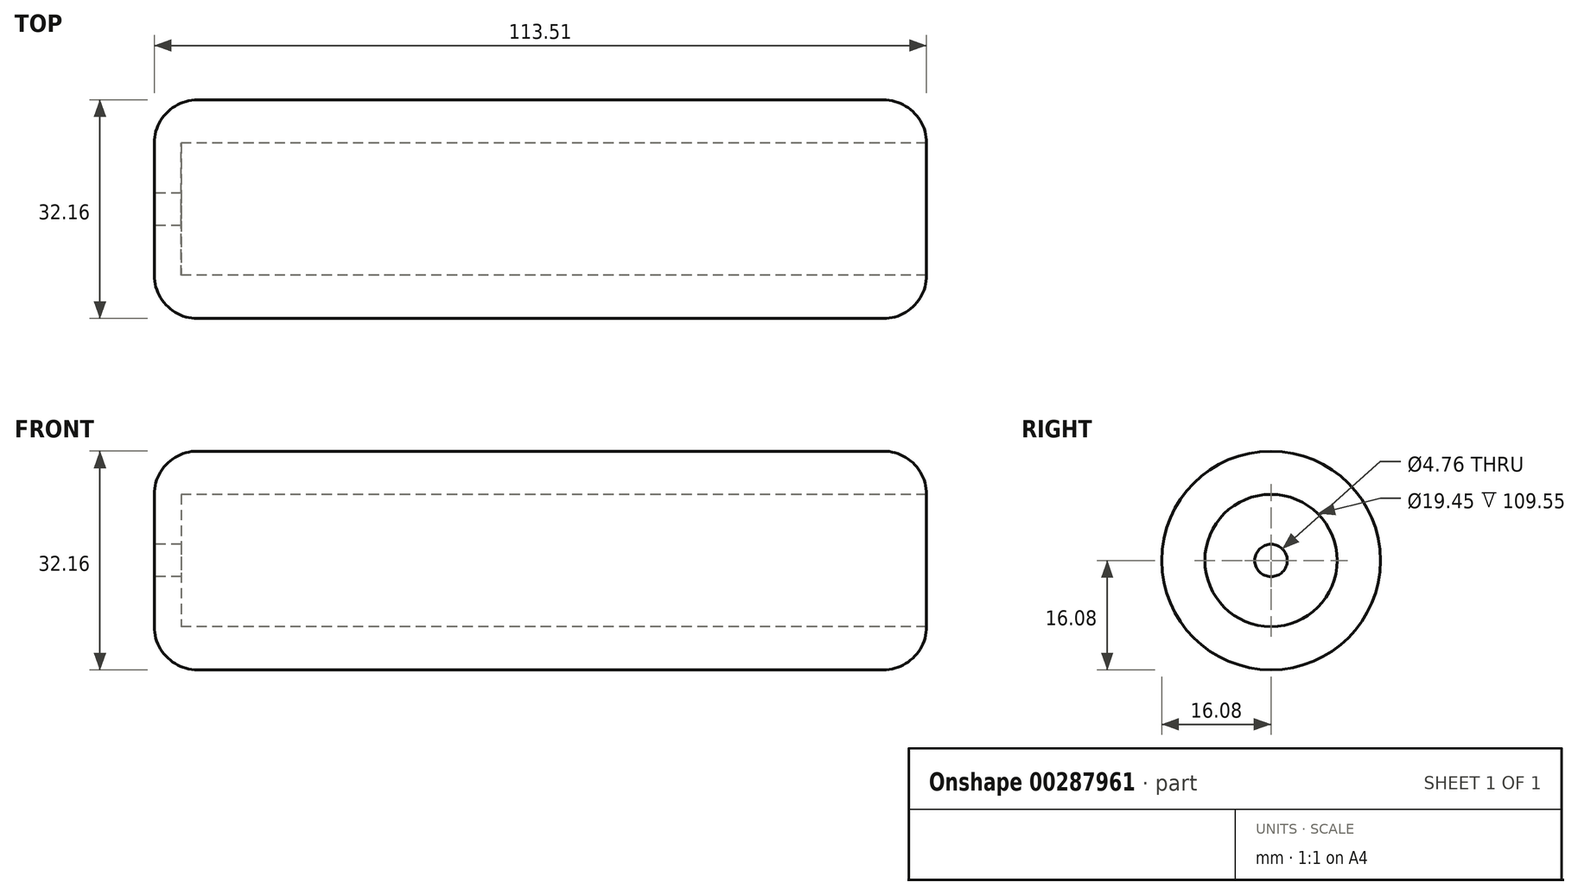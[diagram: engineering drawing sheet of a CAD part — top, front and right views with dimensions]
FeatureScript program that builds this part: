
annotation { "Feature Type Name" : "Feature", "Feature Type Description" : "" }
export const myFeature = defineFeature(function(context is Context, id is Id, definition is map)
    precondition{}
    {
        {
            var Q0;
            Q0=qCreatedBy(makeId("Front.planeOp"),FACE);
            var sketch = newSketch(context, id + "F0", { "sketchPlane" : qUnion([Q0])});
            skLineSegment(sketch, "E0", {"start": v(-39.76, 11.52) * mm, "end": v(69.8, 11.52) * mm});
            skLineSegment(sketch, "E1", {"start": v(69.8, 11.52) * mm, "end": v(69.8, 5.17) * mm});
            skLineSegment(sketch, "E2", {"start": v(69.8, 5.17) * mm, "end": v(-43.72, 5.17) * mm});
            skLineSegment(sketch, "E3", {"start": v(-43.72, 18.87) * mm, "end": v(-39.76, 18.87) * mm});
            skLineSegment(sketch, "E4", {"start": v(-39.76, 18.87) * mm, "end": v(-39.76, 11.52) * mm});
            skLineSegment(sketch, "E5", {"start": v(-43.72, 18.87) * mm, "end": v(-43.72, 5.17) * mm});
            skSolve(sketch);
        }
        {
            var Q0;
            Q0=qCreatedBy(makeId("Front.planeOp"),FACE);
            var sketch = newSketch(context, id + "F1", { "sketchPlane" : qUnion([Q0])});
            skLineSegment(sketch, "E6", {"start": v(-15.6, 21.25) * mm, "end": v(53.48, 21.25) * mm, "construction": true});
            skSolve(sketch);
        }
        {
            var Q0;
            Q0=makeQuery(id+"F0.imprint","IMPRINT",FACE,{"disambiguationData":[TD([[makeQuery(id+"F0.imprint","IMPRINT",EDGE,{"derivedFrom":sQuery(id+"F0.wireOp",EDGE,"E0")}),-1.0]])]});
            var Q1;
            Q1=sQuery(id+"F1.wireOp",EDGE,"E6");
            revolve(context, id + "F2", {"entities" : qUnion([Q0]), "axis" : qUnion([Q1]), "revolveType" : RevolveType.FULL});
        }
        {
            var Q0;
            Q0=makeQuery(id+"F2.opRevolve","SWEPT_EDGE",EDGE,{"disambiguationData":[OSD([sQuery(id+"F0.wireOp",EDGE,"E1"),sQuery(id+"F0.wireOp",EDGE,"E2")])]});
            fillet(context, id + "F3", {"entities" : qUnion([Q0]), "radius" : 6.35 * mm, "tangentPropagation" : true, "allowEdgeOverflow" : false});
        }
        {
            var Q0;
            Q0=makeQuery(id+"F2.opRevolve","SWEPT_EDGE",EDGE,{"disambiguationData":[OSD([sQuery(id+"F0.wireOp",EDGE,"E2"),sQuery(id+"F0.wireOp",EDGE,"E5")])]});
            fillet(context, id + "F4", {"entities" : qUnion([Q0]), "radius" : 6.35 * mm, "tangentPropagation" : true, "allowEdgeOverflow" : false});
        }
    });
